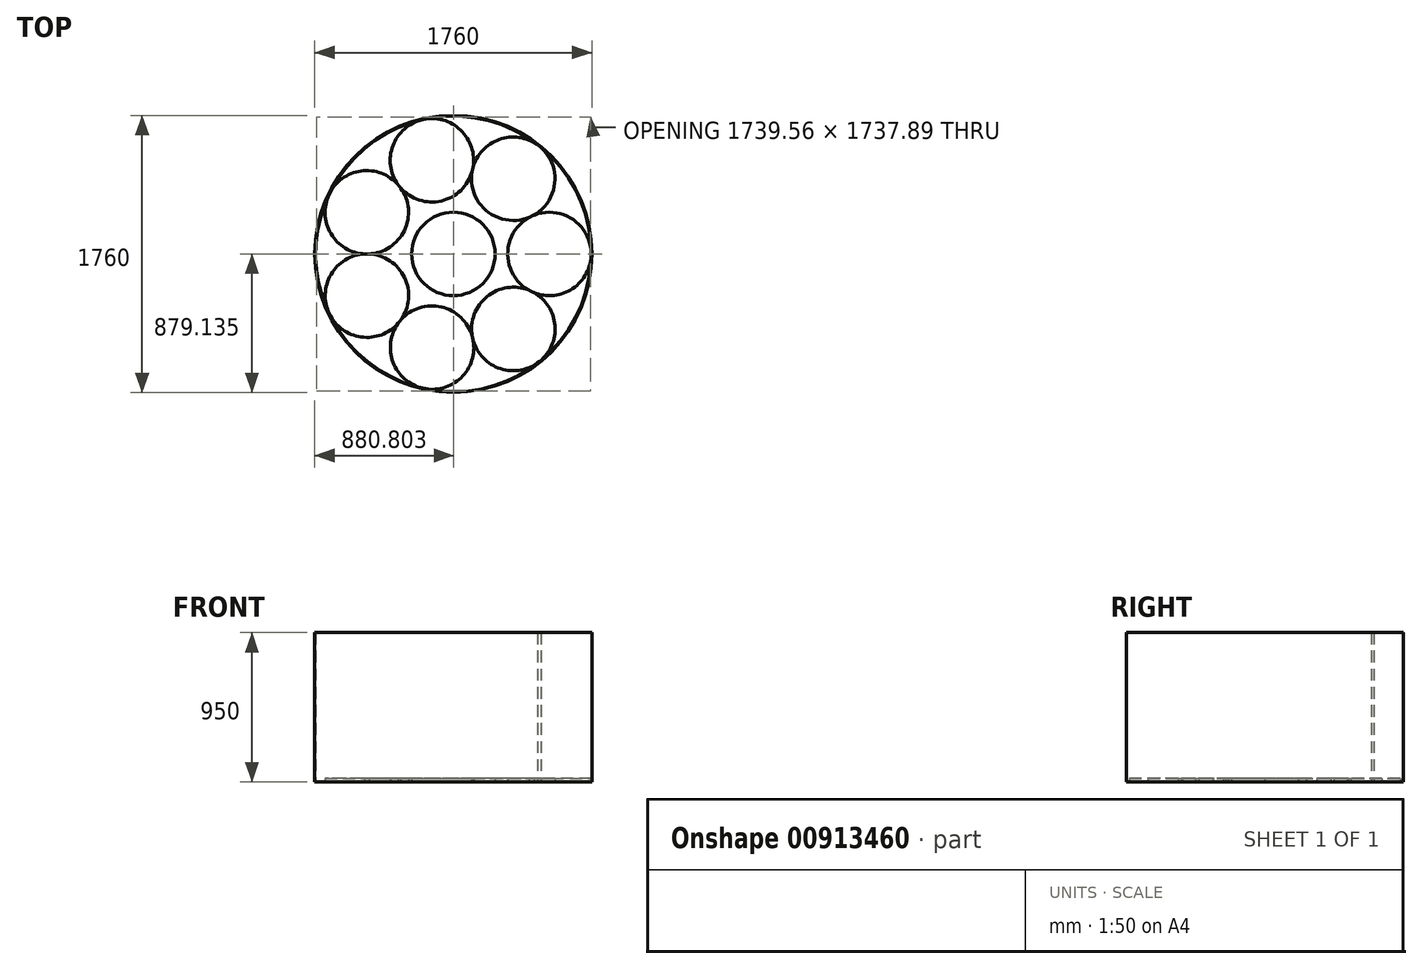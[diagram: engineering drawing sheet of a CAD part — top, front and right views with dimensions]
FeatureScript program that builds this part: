
annotation { "Feature Type Name" : "Feature", "Feature Type Description" : "" }
export const myFeature = defineFeature(function(context is Context, id is Id, definition is map)
    precondition{}
    {
        {
            var Q0;
            Q0=qCreatedBy(makeId("Top.planeOp"),FACE);
            var sketch = newSketch(context, id + "F0", { "sketchPlane" : qUnion([Q0])});
            skCircle(sketch, "E0", {"center": v(-135.18, -594.83) * mm, "radius": 265 * mm});
            skCircle(sketch, "E1", {"center": v(380.77, -476.56) * mm, "radius": 265 * mm});
            skCircle(sketch, "E2", {"center": v(610, 0) * mm, "radius": 265 * mm});
            skCircle(sketch, "E3", {"center": v(380.04, 477.51) * mm, "radius": 265 * mm});
            skCircle(sketch, "E4", {"center": v(-136.31, 594.57) * mm, "radius": 265 * mm});
            skCircle(sketch, "E5", {"center": v(-549.84, 264.14) * mm, "radius": 265 * mm});
            skCircle(sketch, "E6", {"center": v(-549.34, -265.19) * mm, "radius": 265 * mm});
            skCircle(sketch, "E7", {"center": v(0, 0) * mm, "radius": 265 * mm});
            skCircle(sketch, "E8", {"center": v(0, 0) * mm, "radius": 875 * mm});
            skCircle(sketch, "E9", {"center": v(0, 0) * mm, "radius": 880 * mm});
            skSolve(sketch);
        }
        {
            var Q0;
            {var subQ0=sQuery(id+"F0.wireOp",EDGE,"E4");var subQ2=sQuery(id+"F0.wireOp",EDGE,"E3");var subQ3=makeQuery(id+"F0.imprint","INTERSECT",VERTEX,{"disambiguationData":[OD(0.0)],"derivedFrom":[subQ2,subQ0]});Q0=makeQuery(id+"F0.imprint","IMPRINT",FACE,{"disambiguationData":[TD([[makeQuery(id+"F0.imprint","IMPRINT",EDGE,{"disambiguationData":[TD([[subQ3,-1.0]])],"derivedFrom":subQ2}),-1.0]])]});}
            var Q1;
            {var subQ0=sQuery(id+"F0.wireOp",EDGE,"E5");var subQ1=sQuery(id+"F0.wireOp",EDGE,"E4");var subQ7=makeQuery(id+"F0.imprint","INTERSECT",VERTEX,{"disambiguationData":[OD(0.0)],"derivedFrom":[subQ1,subQ0]});Q1=makeQuery(id+"F0.imprint","IMPRINT",FACE,{"disambiguationData":[TD([[makeQuery(id+"F0.imprint","IMPRINT",EDGE,{"disambiguationData":[TD([[subQ7,-1.0]])],"derivedFrom":subQ1}),-1.0]])]});}
            var Q2;
            {var subQ0=sQuery(id+"F0.wireOp",EDGE,"E6");var subQ2=sQuery(id+"F0.wireOp",EDGE,"E0");var subQ7=makeQuery(id+"F0.imprint","INTERSECT",VERTEX,{"disambiguationData":[OD(0.0)],"derivedFrom":[subQ2,subQ0]});Q2=makeQuery(id+"F0.imprint","IMPRINT",FACE,{"disambiguationData":[TD([[makeQuery(id+"F0.imprint","IMPRINT",EDGE,{"disambiguationData":[TD([[subQ7,-1.0]])],"derivedFrom":subQ2}),-1.0]])]});}
            var Q3;
            Q3=makeQuery(id+"F0.imprint","IMPRINT",FACE,{"disambiguationData":[TD([[makeQuery(id+"F0.imprint","IMPRINT",EDGE,{"derivedFrom":sQuery(id+"F0.wireOp",EDGE,"E7")}),1.0]])]});
            var Q4;
            {var subQ0=sQuery(id+"F0.wireOp",EDGE,"E1");var subQ1=sQuery(id+"F0.wireOp",EDGE,"E0");var subQ2=makeQuery(id+"F0.imprint","INTERSECT",VERTEX,{"disambiguationData":[OD(0.0)],"derivedFrom":[subQ1,subQ0]});Q4=makeQuery(id+"F0.imprint","IMPRINT",FACE,{"disambiguationData":[TD([[makeQuery(id+"F0.imprint","IMPRINT",EDGE,{"disambiguationData":[TD([[subQ2,-1.0]])],"derivedFrom":subQ1}),1.0]])]});}
            var Q5;
            {var subQ0=sQuery(id+"F0.wireOp",EDGE,"E1");var subQ4=sQuery(id+"F0.wireOp",EDGE,"E0");var subQ6=makeQuery(id+"F0.imprint","INTERSECT",VERTEX,{"disambiguationData":[OD(0.0)],"derivedFrom":[subQ4,subQ0]});Q5=makeQuery(id+"F0.imprint","IMPRINT",FACE,{"disambiguationData":[TD([[makeQuery(id+"F0.imprint","IMPRINT",EDGE,{"disambiguationData":[TD([[subQ6,1.0]])],"derivedFrom":subQ4}),-1.0]])]});}
            var Q6;
            {var subQ0=sQuery(id+"F0.wireOp",EDGE,"E2");var subQ1=sQuery(id+"F0.wireOp",EDGE,"E1");var subQ2=makeQuery(id+"F0.imprint","INTERSECT",VERTEX,{"disambiguationData":[OD(0.0)],"derivedFrom":[subQ1,subQ0]});Q6=makeQuery(id+"F0.imprint","IMPRINT",FACE,{"disambiguationData":[TD([[makeQuery(id+"F0.imprint","IMPRINT",EDGE,{"disambiguationData":[TD([[subQ2,1.0]])],"derivedFrom":subQ1}),-1.0]])]});}
            var Q7;
            {var subQ0=sQuery(id+"F0.wireOp",EDGE,"E8");var subQ1=sQuery(id+"F0.wireOp",EDGE,"E3");var subQ7=makeQuery(id+"F0.imprint","INTERSECT",VERTEX,{"disambiguationData":[OD(0.0)],"derivedFrom":[subQ1,subQ0]});Q7=makeQuery(id+"F0.imprint","IMPRINT",FACE,{"disambiguationData":[TD([[makeQuery(id+"F0.imprint","IMPRINT",EDGE,{"disambiguationData":[TD([[subQ7,-1.0]])],"derivedFrom":subQ1}),1.0]])]});}
            extrude(context, id + "F1", {"entities" : qUnion([Q0, Q1, Q2, Q3, Q4, Q5, Q6, Q7]), "depth" : 25 * mm, "offsetDistance" : 25 * mm});
        }
        {
            var Q0;
            Q0=makeQuery(id+"F0.imprint","IMPRINT",FACE,{"disambiguationData":[TD([[makeQuery(id+"F0.imprint","IMPRINT",EDGE,{"derivedFrom":sQuery(id+"F0.wireOp",EDGE,"E9")}),1.0]])]});
            extrude(context, id + "F2", {"entities" : qUnion([Q0]), "depth" : 950 * mm, "offsetDistance" : 25 * mm});
        }
    });
